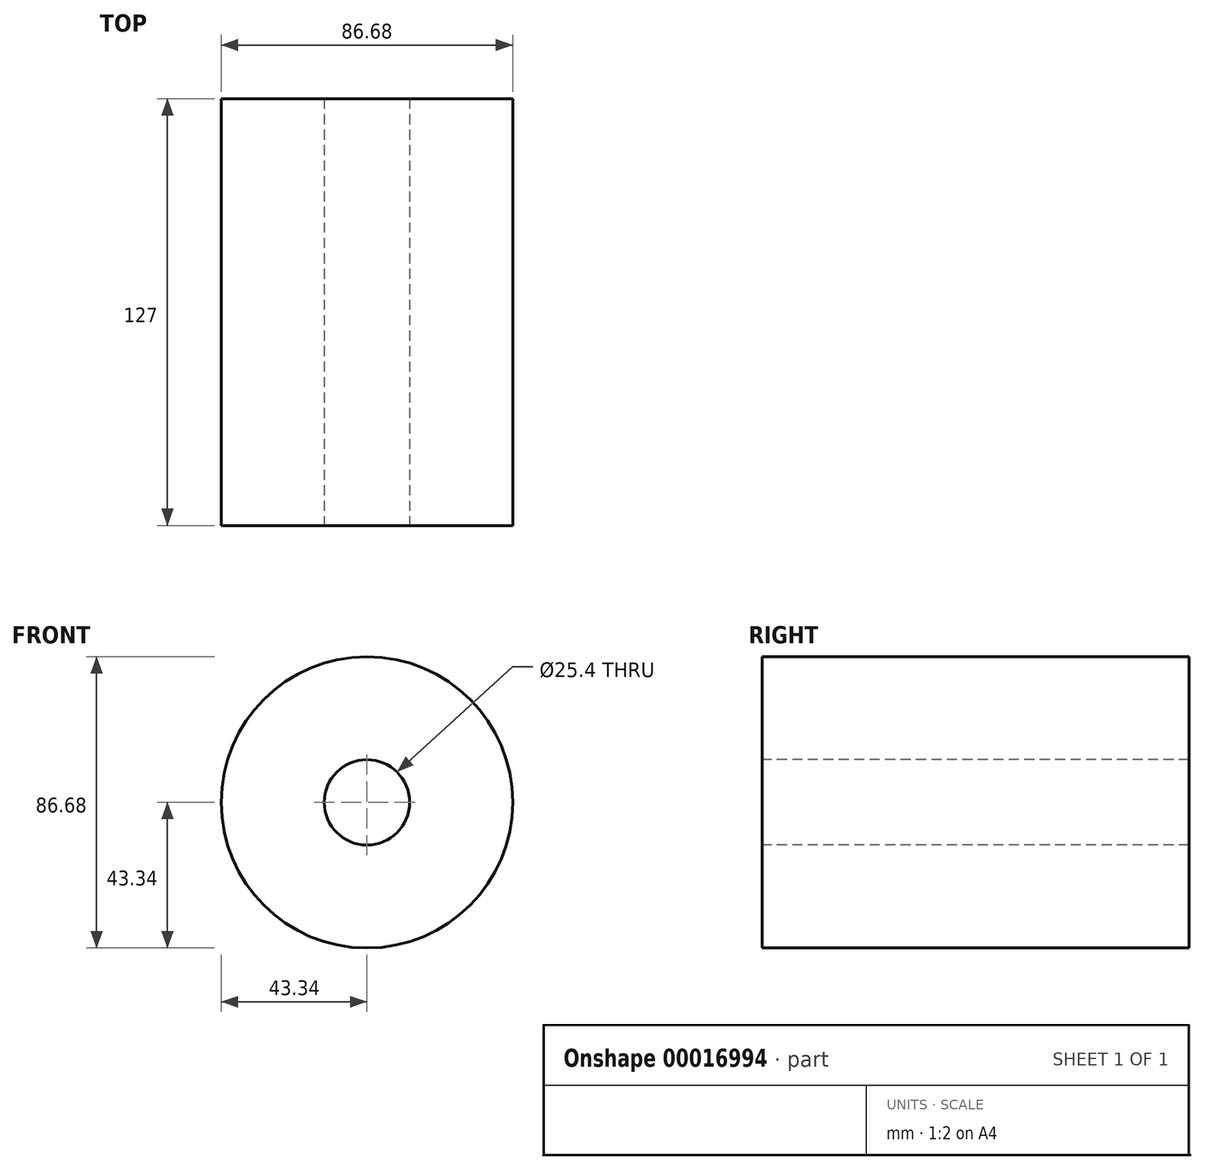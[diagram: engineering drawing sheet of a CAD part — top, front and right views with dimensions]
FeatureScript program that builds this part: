
annotation { "Feature Type Name" : "Feature", "Feature Type Description" : "" }
export const myFeature = defineFeature(function(context is Context, id is Id, definition is map)
    precondition{}
    {
        {
            var Q0;
            Q0=qCreatedBy(makeId("Front.planeOp"),FACE);
            var sketch = newSketch(context, id + "F0", { "sketchPlane" : qUnion([Q0])});
            skCircle(sketch, "E0", {"center": v(0, 0) * mm, "radius": 43.34 * mm});
            skSolve(sketch);
        }
        {
            var Q0;
            Q0=makeQuery(id+"F0.imprint","IMPRINT",FACE,{"disambiguationData":[TD([[makeQuery(id+"F0.imprint","IMPRINT",EDGE,{"derivedFrom":sQuery(id+"F0.wireOp",EDGE,"E0")}),1.0]])]});
            var Q1;
            Q1=qCreatedBy(makeId("Front.planeOp"),FACE);
            extrude(context, id + "F1", {"entities" : qUnion([Q0]), "endBoundEntityFace" : qUnion([Q1]), "depth" : 127 * mm});
        }
        {
            var Q0;
            Q0=makeQuery(id+"F1.opExtrude","CAP_FACE",FACE,{"disambiguationData":[OSD([sQuery(id+"F0.wireOp",EDGE,"E0")])],"isStart":false});
            var sketch = newSketch(context, id + "F2", { "sketchPlane" : qUnion([Q0])});
            skPoint(sketch, "E1", {"position": v(0, 0) * mm});
            skSolve(sketch);
        }
        {
            var Q0;
            Q0=sQuery(id+"F2.wireOp",VERTEX,"E1");
            var Q1;
            Q1=makeQuery(id+"F1.opExtrude","SWEPT_BODY",BODY,{"disambiguationData":[OSD([sQuery(id+"F0.wireOp",EDGE,"E0")])]});
            hole(context, id + "F3", {"style" : HoleStyle.SIMPLE, "holeDiameter" : 25.4 * mm, "endStyle" : HoleEndStyle.THROUGH, "locations" : qUnion([Q0]), "scope" : qUnion([Q1])});
        }
    });
